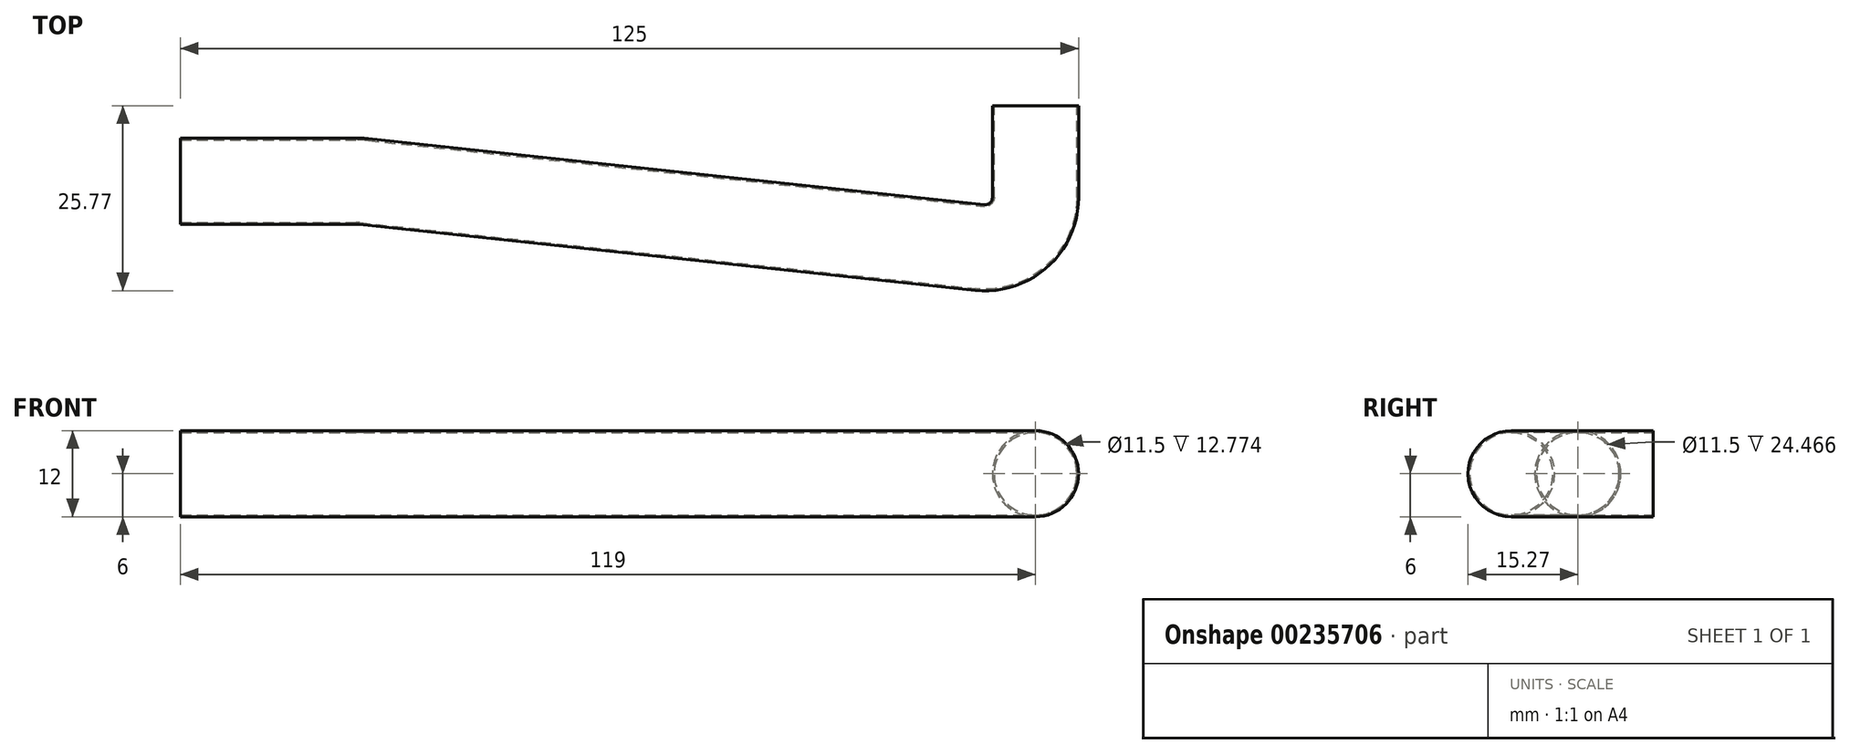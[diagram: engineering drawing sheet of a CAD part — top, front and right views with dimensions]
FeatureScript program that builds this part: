
annotation { "Feature Type Name" : "Feature", "Feature Type Description" : "" }
export const myFeature = defineFeature(function(context is Context, id is Id, definition is map)
    precondition{}
    {
        {
            var Q0;
            Q0=qCreatedBy(makeId("Top.planeOp"),FACE);
            var sketch = newSketch(context, id + "F0", { "sketchPlane" : qUnion([Q0])});
            skLineSegment(sketch, "E0", {"start": v(0, 0) * mm, "end": v(25, 0) * mm, "construction": true});
            skLineSegment(sketch, "E1", {"start": v(0, 0) * mm, "end": v(119, 0) * mm, "construction": true});
            skLineSegment(sketch, "E2", {"start": v(119, 0) * mm, "end": v(119, -15) * mm});
            skLineSegment(sketch, "E3", {"start": v(0, 0) * mm, "end": v(0, -10.5) * mm, "construction": true});
            skArc(sketch, "E4", {"start": v(113.47, -19.97) * mm, "mid": v(117.34, -18.72) * mm, "end": v(119, -15) * mm});
            skLineSegment(sketch, "E5", {"start": v(0, -10.5) * mm, "end": v(24.47, -10.5) * mm});
            skLineSegment(sketch, "E6", {"start": v(25.53, -10.56) * mm, "end": v(113.47, -19.97) * mm});
            skPoint(sketch, "E7.visualSharp", {"position": v(25, -10.5) * mm});
            skArc(sketch, "E7.filletArc", {"start": v(25.53, -10.56) * mm, "mid": v(25, -10.51) * mm, "end": v(24.47, -10.5) * mm});
            skLineSegment(sketch, "E8.0", {"start": v(125, 0) * mm, "end": v(125, -15) * mm});
            skLineSegment(sketch, "E8.1", {"start": v(0, -16.5) * mm, "end": v(24.47, -16.5) * mm});
            skArc(sketch, "E8.2", {"start": v(24.9, -16.52) * mm, "mid": v(24.68, -16.5) * mm, "end": v(24.47, -16.5) * mm});
            skLineSegment(sketch, "E8.3", {"start": v(24.9, -16.52) * mm, "end": v(112.83, -25.94) * mm});
            skArc(sketch, "E8.4", {"start": v(112.83, -25.94) * mm, "mid": v(121.35, -23.18) * mm, "end": v(125, -15) * mm});
            skLineSegment(sketch, "E9.0", {"start": v(0, -4.5) * mm, "end": v(24.47, -4.5) * mm});
            skArc(sketch, "E9.1", {"start": v(26.17, -4.6) * mm, "mid": v(25.32, -4.52) * mm, "end": v(24.47, -4.5) * mm});
            skLineSegment(sketch, "E9.2", {"start": v(26.17, -4.6) * mm, "end": v(111.9, -13.77) * mm});
            skLineSegment(sketch, "E9.3", {"start": v(113, 0) * mm, "end": v(113, -12.77) * mm});
            skPoint(sketch, "E10.visualSharp", {"position": v(113, -13.89) * mm});
            skArc(sketch, "E10.filletArc", {"start": v(111.9, -13.77) * mm, "mid": v(112.67, -13.52) * mm, "end": v(113, -12.77) * mm});
            skLineSegment(sketch, "E11", {"start": v(0, -10.5) * mm, "end": v(0, -4.5) * mm, "construction": true});
            skLineSegment(sketch, "E12", {"start": v(0, -10.5) * mm, "end": v(0, -16.5) * mm, "construction": true});
            skLineSegment(sketch, "E13.0", {"start": v(113.5, 0) * mm, "end": v(113.5, -12.77) * mm});
            skLineSegment(sketch, "E13.1", {"start": v(0, -5) * mm, "end": v(24.47, -5) * mm});
            skArc(sketch, "E13.2", {"start": v(26.12, -5.09) * mm, "mid": v(25.3, -5.02) * mm, "end": v(24.47, -5) * mm});
            skLineSegment(sketch, "E13.3", {"start": v(26.12, -5.09) * mm, "end": v(111.84, -14.27) * mm});
            skArc(sketch, "E13.4", {"start": v(111.84, -14.27) * mm, "mid": v(113, -13.9) * mm, "end": v(113.5, -12.77) * mm});
            skSolve(sketch);
        }
        {
            var Q0;
            Q0=qCreatedBy(makeId("Right.planeOp"),FACE);
            var sketch = newSketch(context, id + "F1", { "sketchPlane" : qUnion([Q0])});
            skLineSegment(sketch, "E14", {"start": v(0, 0) * mm, "end": v(-10.5, 0) * mm});
            skCircle(sketch, "E15", {"center": v(-10.5, 0) * mm, "radius": 6 * mm});
            skCircle(sketch, "E16", {"center": v(-10.5, 0) * mm, "radius": 5.75 * mm});
            skSolve(sketch);
        }
        {
            var Q0;
            Q0=makeQuery(id+"F1.imprint","IMPRINT",FACE,{"disambiguationData":[TD([[makeQuery(id+"F1.imprint","IMPRINT",EDGE,{"derivedFrom":sQuery(id+"F1.wireOp",EDGE,"E15")}),1.0]])]});
            var Q1;
            Q1=sQuery(id+"F0.wireOp",EDGE,"E9.0");
            var Q2;
            Q2=sQuery(id+"F0.wireOp",EDGE,"E9.1");
            var Q3;
            Q3=sQuery(id+"F0.wireOp",EDGE,"E9.2");
            var Q4;
            Q4=sQuery(id+"F0.wireOp",EDGE,"E10.filletArc");
            var Q5;
            Q5=sQuery(id+"F0.wireOp",EDGE,"E9.3");
            sweep(context, id + "F2", {"profiles" : qUnion([Q0]), "path" : qUnion([Q1, Q2, Q3, Q4, Q5])});
        }
    });
